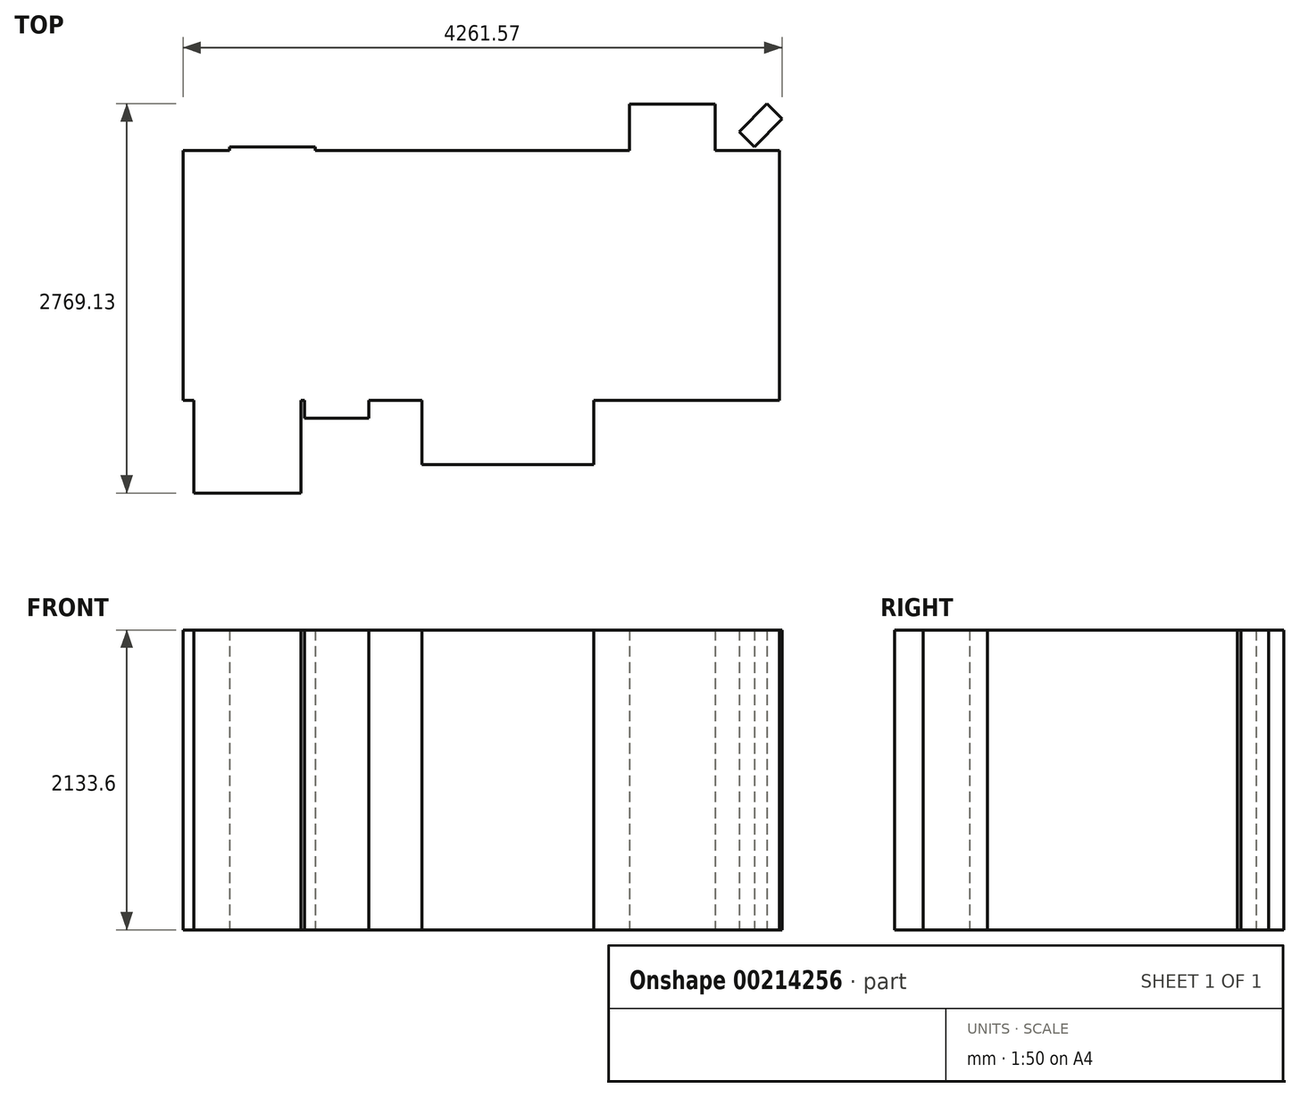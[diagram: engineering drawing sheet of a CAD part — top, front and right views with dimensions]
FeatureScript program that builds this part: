
annotation { "Feature Type Name" : "Feature", "Feature Type Description" : "" }
export const myFeature = defineFeature(function(context is Context, id is Id, definition is map)
    precondition{}
    {
        {
            var Q0;
            Q0=qCreatedBy(makeId("Top.planeOp"),FACE);
            var sketch = newSketch(context, id + "F0", { "sketchPlane" : qUnion([Q0])});
            skLineSegment(sketch, "E0.bottom", {"start": v(-2120.9, 889) * mm, "end": v(2120.9, 889) * mm});
            skLineSegment(sketch, "E0.top", {"start": v(-2120.9, -889) * mm, "end": v(2120.9, -889) * mm});
            skLineSegment(sketch, "E0.left", {"start": v(-2120.9, 889) * mm, "end": v(-2120.9, -889) * mm});
            skLineSegment(sketch, "E0.right", {"start": v(2120.9, 889) * mm, "end": v(2120.9, -889) * mm});
            skLineSegment(sketch, "E1", {"start": v(-2120.9, 0) * mm, "end": v(2120.9, 0) * mm, "construction": true});
            skLineSegment(sketch, "E2", {"start": v(0, 889) * mm, "end": v(0, -889) * mm, "construction": true});
            skLineSegment(sketch, "E3", {"start": v(-2044.7, -889) * mm, "end": v(-2044.7, -1549.4) * mm});
            skLineSegment(sketch, "E4", {"start": v(-2044.7, -1549.4) * mm, "end": v(-1282.7, -1549.4) * mm});
            skLineSegment(sketch, "E5", {"start": v(-1282.7, -1549.4) * mm, "end": v(-1282.7, -889) * mm});
            skLineSegment(sketch, "E6", {"start": v(-419.1, -889) * mm, "end": v(-419.1, -1346.2) * mm});
            skLineSegment(sketch, "E7", {"start": v(-419.1, -1346.2) * mm, "end": v(800.1, -1346.2) * mm});
            skLineSegment(sketch, "E8", {"start": v(800.1, -1346.2) * mm, "end": v(800.1, -889) * mm});
            skLineSegment(sketch, "E9", {"start": v(1663.7, 889) * mm, "end": v(1663.7, 1219.2) * mm});
            skLineSegment(sketch, "E10", {"start": v(1663.7, 1219.2) * mm, "end": v(1054.1, 1219.2) * mm});
            skLineSegment(sketch, "E11", {"start": v(1054.1, 1219.2) * mm, "end": v(1054.1, 889) * mm});
            skLineSegment(sketch, "E12", {"start": v(-1790.7, 889) * mm, "end": v(-1790.7, 914.4) * mm});
            skLineSegment(sketch, "E13", {"start": v(-1790.7, 914.4) * mm, "end": v(-1181.1, 914.4) * mm});
            skLineSegment(sketch, "E14", {"start": v(-1181.1, 914.4) * mm, "end": v(-1181.1, 889) * mm});
            skLineSegment(sketch, "E15", {"start": v(-1257.3, -889) * mm, "end": v(-1257.3, -1016) * mm});
            skLineSegment(sketch, "E16", {"start": v(-1257.3, -1016) * mm, "end": v(-800.1, -1016) * mm});
            skLineSegment(sketch, "E17", {"start": v(-800.1, -1016) * mm, "end": v(-800.1, -889) * mm});
            skLineSegment(sketch, "E18", {"start": v(1835.34, 1022.16) * mm, "end": v(2032.9, 1219.73) * mm});
            skLineSegment(sketch, "E19", {"start": v(2032.9, 1219.73) * mm, "end": v(2140.67, 1111.97) * mm});
            skLineSegment(sketch, "E20", {"start": v(2140.67, 1111.97) * mm, "end": v(1943.1, 914.4) * mm});
            skLineSegment(sketch, "E21", {"start": v(1943.1, 914.4) * mm, "end": v(1835.34, 1022.16) * mm});
            skSolve(sketch);
        }
        {
            var Q0;
            {var subQ3=sQuery(id+"F0.wireOp",EDGE,"E0.left");Q0=makeQuery(id+"F0.imprint","IMPRINT",FACE,{"disambiguationData":[TD([[makeQuery(id+"F0.imprint","IMPRINT",EDGE,{"derivedFrom":subQ3}),1.0]])]});}
            var Q1;
            {var subQ0=sQuery(id+"F0.wireOp",EDGE,"E12");Q1=makeQuery(id+"F0.imprint","IMPRINT",FACE,{"disambiguationData":[TD([[makeQuery(id+"F0.imprint","IMPRINT",EDGE,{"derivedFrom":subQ0}),-1.0]])]});}
            var Q2;
            {var subQ0=sQuery(id+"F0.wireOp",EDGE,"E9");Q2=makeQuery(id+"F0.imprint","IMPRINT",FACE,{"disambiguationData":[TD([[makeQuery(id+"F0.imprint","IMPRINT",EDGE,{"derivedFrom":subQ0}),1.0]])]});}
            var Q3;
            {var subQ0=sQuery(id+"F0.wireOp",EDGE,"E6");Q3=makeQuery(id+"F0.imprint","IMPRINT",FACE,{"disambiguationData":[TD([[makeQuery(id+"F0.imprint","IMPRINT",EDGE,{"derivedFrom":subQ0}),1.0]])]});}
            var Q4;
            {var subQ0=sQuery(id+"F0.wireOp",EDGE,"E3");Q4=makeQuery(id+"F0.imprint","IMPRINT",FACE,{"disambiguationData":[TD([[makeQuery(id+"F0.imprint","IMPRINT",EDGE,{"derivedFrom":subQ0}),1.0]])]});}
            var Q5;
            {var subQ0=sQuery(id+"F0.wireOp",EDGE,"E15");Q5=makeQuery(id+"F0.imprint","IMPRINT",FACE,{"disambiguationData":[TD([[makeQuery(id+"F0.imprint","IMPRINT",EDGE,{"derivedFrom":subQ0}),1.0]])]});}
            var Q6;
            Q6=makeQuery(id+"F0.imprint","IMPRINT",FACE,{"disambiguationData":[TD([[makeQuery(id+"F0.imprint","IMPRINT",EDGE,{"derivedFrom":sQuery(id+"F0.wireOp",EDGE,"E18")}),-1.0]])]});
            extrude(context, id + "F1", {"entities" : qUnion([Q0, Q1, Q2, Q3, Q4, Q5, Q6]), "depth" : 2133.6 * mm});
        }
    });
